# Revit family: IS_Multisuite_A2305_BIM_IT
name_source: partatom
category: Plumbing Fixtures
revit_build: Autodesk Revit 2017 (Build: 20160225_1515(x64)
units: mm (PartAtom-declared; Revit-internal decimal feet)

## family parameters
Always vertical = No
Cut with Voids When Loaded = No
OmniClass Number = 23.45.05.14.21.11
OmniClass Title = Bath/Shower Units
Part Type = Normal
Room Calculation Point = No
Round Connector Dimension = Use Diameter
Shared = No
Work Plane-Based = No

## types (2) — shared parameters
Accessori = www.idealstandard.it
AltezzaNominale = 178 mm
BIMobject category = Shower Channel
BIMobject category code = sanitary-shower-channel
BIMobject main category = Sanitary
BIMobject main category code = sanitary
BOSUseNativeGeometries = 1
Brand = Ideal Standard
Brand url = http://www.idealstandard.it
CodiceABarre = 4015413361538
CodiceDiPrestazione = EN
Connessione = piombatura
Date of publishing = 2019_01_04
EAN code = https://4015413361538
Edition number = 1
Forma = scolpito
Garanzia = Garanzia Ideal Standard
Grado = n/s
IFC Classification = IfcSanitaryTerminal
IfcEsportaCome = SanitaryTerminal
InformazioniDiProdotto = http://www.idealstandard.it
Installation instructions = http://www.idealstandard.it
Installazione = http://www.idealstandard.it
InstruzioniInstallazione = http://www.idealstandard.it
LunghezzaNominale = 268 mm
Maniglia = No
Manufacturer name = Ideal Standard
Material main = Brass
Materiale = Ottone
NBS Reference Code = Pr_70_55_96_97
NBS Reference Description = Wash Basin Wastes
NominalHeight = 178 mm
NominalLength = 268 mm
NominalWidth = 66 mm  [stored 0.216535 ft]
OmniClass Code = 23-31 17 00
OmniClass Description = Showers
PartiDiRicambio = http://www.idealstandard.it
PiattoDoccia = No
Product Guid = d7743e3d-78e8-4474-be6d-471af223c59e
Product SKU = A2305
Product certification = http://www.idealstandard.it
Product data url = https://bimobject.com
Product family = OTHER
Product group = Washbasin taps
Product name = TUBING TRAP 1 1/4" FOR BASIN WHITE
Product url = http://www.idealstandard.it
QR code = http://bimobject.com
Revisione = 1
RiferimentoClassificazioneUni2015 = SL_35_80_80
Size = 178 x 268 x 66mm
Technical description = http://www.idealstandard.it
Telefono = 800 652 290
TipoDiDato = Fisso
TipoEspotazioneIfc = IfcSanitaryTerminalType
URL = http://www.idealstandard.it
Uniclass 1.4 Code = L7214
Uniclass 1.4 Description = Showers
Uniclass 2.0 Code = PR-35-06-84
Uniclass 2.0 Description = Shower Trays
Uniclass 2015 Code = SL_35_80_80
Uniclass 2015 Name = Showers
UnitàDurata = anni
UnitàDurataGaranzia = anni
UnitàLineare = millimetri
UnitàMonetaria = €
UnitàSuperficie = €
UnitàVolume = millimetri
Versione = 1
VersioneClassificazioneUni2015 = 1
Youtube clip = https://www.youtube.com
zero-valued in all types: CostoDiSostituzione, DimensioneScarico, LarghezzaNominale, Nominal depth, Nominal height, ProfonditaNominale, SeatMaterial, SpessoreDelMateriale, SpilloverLivello, Weight Net (Kg)

## per-type parameters (varying)
| type | Caratteristiche | Colore | Description | Desrizione | Finitura | Model | NumeroDiModello |
| A2305AA - TUBING TRAP 1 1/4 FOR BASIN CHROME | TUBING TRAP 1 1/4 FOR BASIN    CHROME | Cromo | TUBING TRAP 1 1/4 FOR BASIN    CHROME | TUBING TRAP 1 1/4 FOR BASIN    CHROME | Cromo | A2305AA | A6662AA |
| A2305AC - TUBING TRAP 1 1/4" FOR BASIN WHITE | TUBING TRAP 1 1/4" FOR BASIN    WHITE | Bianco | TUBING TRAP 1 1/4" FOR BASIN    WHITE | TUBING TRAP 1 1/4" FOR BASIN    WHITE | Bianco | A2305AC | A2305AA |

note: [stored X ft] marks values corroborated as IEEE doubles in the binary element streams (Revit-internal decimal feet)

## geometry (parser evidence)
native form markers: Sweep x3
no freeform markers — native parametric forms only
